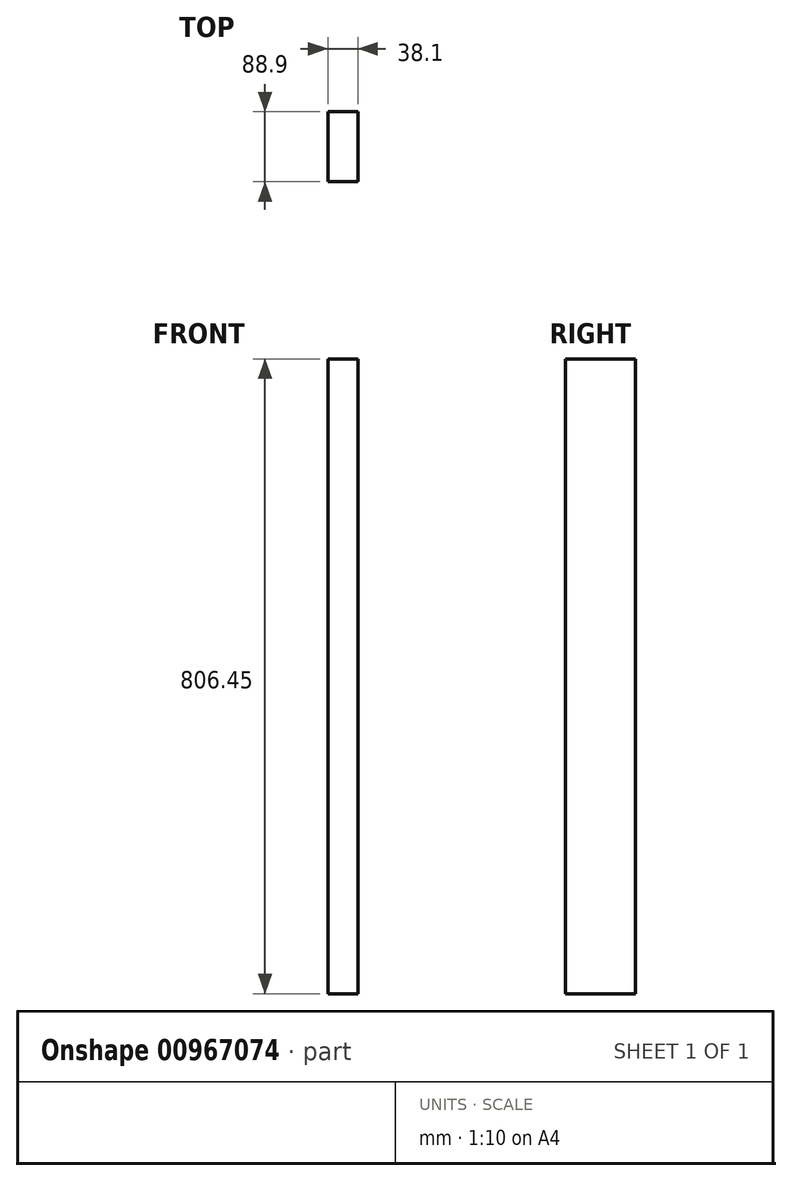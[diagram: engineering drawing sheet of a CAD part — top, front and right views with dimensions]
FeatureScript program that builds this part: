
annotation { "Feature Type Name" : "Feature", "Feature Type Description" : "" }
export const myFeature = defineFeature(function(context is Context, id is Id, definition is map)
    precondition{}
    {
        {
            var Q0;
            Q0=qCreatedBy(makeId("Top.planeOp"),FACE);
            var sketch = newSketch(context, id + "F0", { "sketchPlane" : qUnion([Q0])});
            skLineSegment(sketch, "E0.bottom", {"start": v(0, 0) * mm, "end": v(-38.1, 0) * mm});
            skLineSegment(sketch, "E0.top", {"start": v(0, 88.9) * mm, "end": v(-38.1, 88.9) * mm});
            skLineSegment(sketch, "E0.left", {"start": v(0, 0) * mm, "end": v(0, 88.9) * mm});
            skLineSegment(sketch, "E0.right", {"start": v(-38.1, 0) * mm, "end": v(-38.1, 88.9) * mm});
            skSolve(sketch);
        }
        {
            var Q0;
            Q0 = qSketchRegion(id + "F0", true);
            extrude(context, id + "F1", {"entities" : qUnion([Q0]), "depth" : 806.45 * mm, "offsetDistance" : 25.4 * mm});
        }
    });
